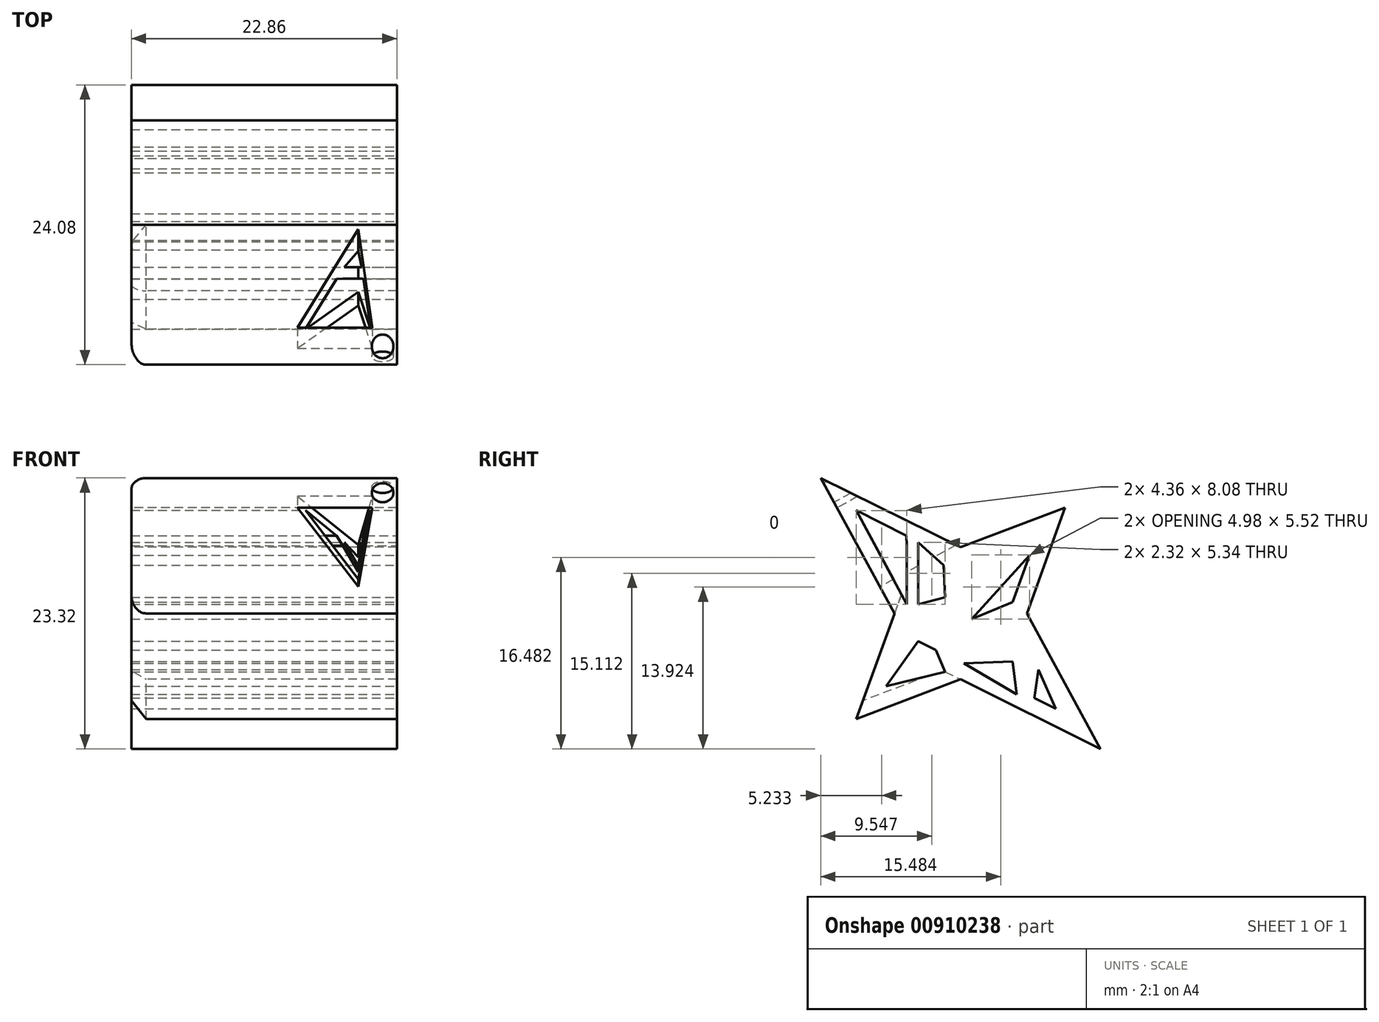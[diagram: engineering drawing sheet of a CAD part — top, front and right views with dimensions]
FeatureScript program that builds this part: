
annotation { "Feature Type Name" : "Feature", "Feature Type Description" : "" }
export const myFeature = defineFeature(function(context is Context, id is Id, definition is map)
    precondition{}
    {
        {
            var Q0;
            Q0=qCreatedBy(makeId("Right.planeOp"),FACE);
            var sketch = newSketch(context, id + "F0", { "sketchPlane" : qUnion([Q0])});
            skPoint(sketch, "E0.middle", {"position": v(0, 0) * mm});
            skLineSegment(sketch, "E1", {"start": v(-12.04, 11.66) * mm, "end": v(-5.68, 0) * mm});
            skLineSegment(sketch, "E2", {"start": v(-8.99, -9.1) * mm, "end": v(-5.68, 0) * mm});
            skLineSegment(sketch, "E3", {"start": v(-8.99, -9.1) * mm, "end": v(0, -5.68) * mm});
            skLineSegment(sketch, "E4", {"start": v(0, -5.68) * mm, "end": v(12.04, -11.66) * mm});
            skLineSegment(sketch, "E5", {"start": v(5.7, 0) * mm, "end": v(12.04, -11.66) * mm});
            skLineSegment(sketch, "E6", {"start": v(5.7, 0) * mm, "end": v(8.99, 9.1) * mm});
            skLineSegment(sketch, "E7", {"start": v(0, 5.7) * mm, "end": v(8.99, 9.1) * mm});
            skLineSegment(sketch, "E8", {"start": v(-12.04, 11.66) * mm, "end": v(0, 5.7) * mm});
            skSolve(sketch);
        }
        {
            var Q0;
            Q0 = qSketchRegion(id + "F0", true);
            extrude(context, id + "F1", {"entities" : qUnion([Q0]), "depth" : 22.86 * mm, "offsetDistance" : 25.4 * mm});
        }
        {
            var Q0;
            Q0=makeQuery(id+"F1.opExtrude","CAP_FACE",FACE,{"disambiguationData":[OSD([sQuery(id+"F0.wireOp",EDGE,"E1"),sQuery(id+"F0.wireOp",EDGE,"E2"),sQuery(id+"F0.wireOp",EDGE,"E3"),sQuery(id+"F0.wireOp",EDGE,"E4"),sQuery(id+"F0.wireOp",EDGE,"E5"),sQuery(id+"F0.wireOp",EDGE,"E6"),sQuery(id+"F0.wireOp",EDGE,"E7"),sQuery(id+"F0.wireOp",EDGE,"E8")])],"isStart":false});
            var sketch = newSketch(context, id + "F2", { "sketchPlane" : qUnion([Q0])});
            skPoint(sketch, "E9.startSnap0", {"position": v(8.87, -5.83) * mm});
            skLineSegment(sketch, "E10", {"start": v(6.69, -4.84) * mm, "end": v(6.34, -7.27) * mm});
            skLineSegment(sketch, "E11", {"start": v(4.84, -6.97) * mm, "end": v(4.47, -4.15) * mm});
            skLineSegment(sketch, "E12", {"start": v(0.3, -4.3) * mm, "end": v(4.47, -4.15) * mm});
            skLineSegment(sketch, "E13", {"start": v(4.84, -3.15) * mm, "end": v(-0.46, -3.15) * mm});
            skLineSegment(sketch, "E14", {"start": v(-0.46, -3.15) * mm, "end": v(4.84, -3.15) * mm});
            skLineSegment(sketch, "E15", {"start": v(4.84, -3.15) * mm, "end": v(4.22, -0.5) * mm});
            skLineSegment(sketch, "E16", {"start": v(-0.46, -3.15) * mm, "end": v(4.22, -0.5) * mm});
            skLineSegment(sketch, "E17", {"start": v(4.47, 0.96) * mm, "end": v(5.93, 5.02) * mm});
            skLineSegment(sketch, "E18", {"start": v(5.93, 5.02) * mm, "end": v(0.95, -0.5) * mm});
            skLineSegment(sketch, "E19", {"start": v(4.47, 0.96) * mm, "end": v(0.95, -0.5) * mm});
            skLineSegment(sketch, "E20", {"start": v(5.2, 6.12) * mm, "end": v(0, 4.16) * mm});
            skLineSegment(sketch, "E21", {"start": v(0, 4.16) * mm, "end": v(5.2, 6.12) * mm});
            skLineSegment(sketch, "E22", {"start": v(5.2, 6.12) * mm, "end": v(0, 1.38) * mm});
            skLineSegment(sketch, "E23", {"start": v(0, 4.16) * mm, "end": v(0, 1.38) * mm});
            skLineSegment(sketch, "E24", {"start": v(-1.33, 1.38) * mm, "end": v(-1.47, 4.16) * mm});
            skLineSegment(sketch, "E25", {"start": v(-1.47, 4.16) * mm, "end": v(-3.65, 6.12) * mm});
            skLineSegment(sketch, "E26", {"start": v(-3.65, 6.12) * mm, "end": v(-3.65, 0.78) * mm});
            skLineSegment(sketch, "E27", {"start": v(-1.33, 1.38) * mm, "end": v(-3.65, 0.78) * mm});
            skLineSegment(sketch, "E28", {"start": v(-1.33, -5.01) * mm, "end": v(-2.14, -3.15) * mm});
            skLineSegment(sketch, "E29", {"start": v(-2.14, -3.15) * mm, "end": v(-3.65, -2.38) * mm});
            skLineSegment(sketch, "E30", {"start": v(-3.65, -2.38) * mm, "end": v(-6.4, -6.26) * mm});
            skLineSegment(sketch, "E31", {"start": v(-6.4, -6.26) * mm, "end": v(-1.33, -5.01) * mm});
            skLineSegment(sketch, "E32", {"start": v(-4.63, 0.78) * mm, "end": v(-4.63, 5.83) * mm});
            skPoint(sketch, "E32.endSnap0", {"position": v(-8.86, 5.83) * mm});
            skLineSegment(sketch, "E33", {"start": v(-4.63, 5.83) * mm, "end": v(-4.66, 6.7) * mm});
            skLineSegment(sketch, "E34", {"start": v(-4.66, 6.7) * mm, "end": v(-8.99, 8.86) * mm});
            skLineSegment(sketch, "E35", {"start": v(-8.99, 8.86) * mm, "end": v(-4.63, 0.78) * mm});
            skLineSegment(sketch, "E36", {"start": v(4.84, -6.97) * mm, "end": v(0.3, -4.3) * mm});
            skLineSegment(sketch, "E37", {"start": v(-8.99, 8.86) * mm, "end": v(-10.17, 8.22) * mm, "construction": true});
            skLineSegment(sketch, "E38", {"start": v(-4.03, 0) * mm, "end": v(-4.63, 0.78) * mm, "construction": true});
            skLineSegment(sketch, "E39", {"start": v(-4.63, 4.78) * mm, "end": v(-3.65, 4.78) * mm, "construction": true});
            skPoint(sketch, "E39.endSnap0", {"position": v(-3.65, 3.45) * mm});
            skLineSegment(sketch, "E40", {"start": v(-1.4, 2.78) * mm, "end": v(0, 2.78) * mm, "construction": true});
            skLineSegment(sketch, "E41", {"start": v(1.53, 2.78) * mm, "end": v(2.73, 1.47) * mm, "construction": true});
            skLineSegment(sketch, "E42", {"start": v(4.47, -1.56) * mm, "end": v(6.31, -1.13) * mm, "construction": true});
            skLineSegment(sketch, "E43", {"start": v(6.34, -7.27) * mm, "end": v(8.19, -8.19) * mm});
            skLineSegment(sketch, "E44", {"start": v(6.69, -4.84) * mm, "end": v(8.19, -8.19) * mm});
            skLineSegment(sketch, "E45", {"start": v(-4.03, 0) * mm, "end": v(-1.14, -2.06) * mm});
            skLineSegment(sketch, "E46", {"start": v(-1.14, -2.06) * mm, "end": v(-4.03, 0) * mm});
            skLineSegment(sketch, "E47", {"start": v(-4.03, 0) * mm, "end": v(-0.2, -0.5) * mm});
            skLineSegment(sketch, "E48", {"start": v(-0.2, -0.5) * mm, "end": v(-1.14, -2.06) * mm});
            skSolve(sketch);
        }
        {
            var Q0;
            Q0=makeQuery(id+"F2.imprint","IMPRINT",FACE,{"disambiguationData":[TD([[makeQuery(id+"F2.imprint","IMPRINT",EDGE,{"derivedFrom":sQuery(id+"F2.wireOp",EDGE,"nE2Qsl0X-DvAB-Qw5M-Smw6-ZWJYBDrrcIoU")}),1.0]])]});
            var Q1;
            Q1=makeQuery(id+"F2.imprint","IMPRINT",FACE,{"disambiguationData":[TD([[makeQuery(id+"F2.imprint","IMPRINT",EDGE,{"derivedFrom":sQuery(id+"F2.wireOp",EDGE,"E11")}),1.0]])]});
            var Q2;
            Q2=makeQuery(id+"F2.imprint","IMPRINT",FACE,{"disambiguationData":[TD([[makeQuery(id+"F2.imprint","IMPRINT",EDGE,{"derivedFrom":sQuery(id+"F2.wireOp",EDGE,"E14")}),1.0]])]});
            var Q3;
            Q3=makeQuery(id+"F2.imprint","IMPRINT",FACE,{"disambiguationData":[TD([[makeQuery(id+"F2.imprint","IMPRINT",EDGE,{"derivedFrom":sQuery(id+"F2.wireOp",EDGE,"E28")}),1.0]])]});
            var Q4;
            Q4=makeQuery(id+"F2.imprint","IMPRINT",FACE,{"disambiguationData":[TD([[makeQuery(id+"F2.imprint","IMPRINT",EDGE,{"derivedFrom":sQuery(id+"F2.wireOp",EDGE,"V6S1NtYD-F1rM-hO7p-zKYz-p3XUJGEGcDZX")}),1.0]])]});
            var Q5;
            Q5=makeQuery(id+"F2.imprint","IMPRINT",FACE,{"disambiguationData":[TD([[makeQuery(id+"F2.imprint","IMPRINT",EDGE,{"derivedFrom":sQuery(id+"F2.wireOp",EDGE,"E24")}),1.0]])]});
            var Q6;
            Q6=makeQuery(id+"F2.imprint","IMPRINT",FACE,{"disambiguationData":[TD([[makeQuery(id+"F2.imprint","IMPRINT",EDGE,{"derivedFrom":sQuery(id+"F2.wireOp",EDGE,"E32")}),1.0]])]});
            var Q7;
            Q7=makeQuery(id+"F2.imprint","IMPRINT",FACE,{"disambiguationData":[TD([[makeQuery(id+"F2.imprint","IMPRINT",EDGE,{"derivedFrom":sQuery(id+"F2.wireOp",EDGE,"1S0bT3UO-28IP-Q8NI-ZD6i-Laru1sXz17AQ")}),1.0]])]});
            var Q8;
            Q8=makeQuery(id+"F2.imprint","IMPRINT",FACE,{"disambiguationData":[TD([[makeQuery(id+"F2.imprint","IMPRINT",EDGE,{"derivedFrom":sQuery(id+"F2.wireOp",EDGE,"E17")}),1.0]])]});
            var Q9;
            Q9=makeQuery(id+"F2.imprint","IMPRINT",FACE,{"disambiguationData":[TD([[makeQuery(id+"F2.imprint","IMPRINT",EDGE,{"derivedFrom":sQuery(id+"F2.wireOp",EDGE,"E21")}),-1.0]])]});
            var Q10;
            Q10=makeQuery(id+"F2.imprint","IMPRINT",FACE,{"disambiguationData":[TD([[makeQuery(id+"F2.imprint","IMPRINT",EDGE,{"derivedFrom":sQuery(id+"F2.wireOp",EDGE,"E46")}),-1.0]])]});
            var Q11;
            Q11=makeQuery(id+"F2.imprint","IMPRINT",FACE,{"disambiguationData":[TD([[makeQuery(id+"F2.imprint","IMPRINT",EDGE,{"derivedFrom":sQuery(id+"F2.wireOp",EDGE,"E10")}),1.0]])]});
            extrude(context, id + "F3", {"entities" : qUnion([Q0, Q1, Q2, Q3, Q4, Q5, Q6, Q7, Q8, Q9, Q10, Q11]), "operationType" : NewBodyOperationType.REMOVE, "endBound" : BoundingType.THROUGH_ALL, "oppositeDirection" : true, "depth" : 25.4 * mm, "offsetDistance" : 25.4 * mm});
        }
        {
            var Q0;
            Q0=makeQuery(id+"F1.opExtrude","SWEPT_FACE",FACE,{"disambiguationData":[OSD([sQuery(id+"F0.wireOp",EDGE,"E1")])]});
            var sketch = newSketch(context, id + "F4", { "sketchPlane" : qUnion([Q0])});
            skLineSegment(sketch, "E49", {"start": v(14.3, 13.08) * mm, "end": v(20.74, 13.08) * mm});
            skLineSegment(sketch, "E50", {"start": v(20.74, 13.08) * mm, "end": v(19.53, 5.35) * mm});
            skLineSegment(sketch, "E51", {"start": v(19.53, 5.35) * mm, "end": v(14.3, 13.08) * mm});
            skSolve(sketch);
        }
        {
            var Q0;
            Q0=makeQuery(id+"F4.imprint","IMPRINT",FACE,{"disambiguationData":[TD([[makeQuery(id+"F4.imprint","IMPRINT",EDGE,{"derivedFrom":sQuery(id+"F4.wireOp",EDGE,"E49")}),-1.0]])]});
            extrude(context, id + "F5", {"entities" : qUnion([Q0]), "operationType" : NewBodyOperationType.REMOVE, "endBound" : BoundingType.THROUGH_ALL, "oppositeDirection" : true, "depth" : 25.4 * mm, "offsetDistance" : 25.4 * mm});
        }
        {
            var Q0;
            Q0=makeQuery(id+"F1.opExtrude","SWEPT_FACE",FACE,{"disambiguationData":[OSD([sQuery(id+"F0.wireOp",EDGE,"E1")])]});
            var sketch = newSketch(context, id + "F6", { "sketchPlane" : qUnion([Q0])});
            skCircle(sketch, "E52", {"center": v(21.62, 14.56) * mm, "radius": 0.93 * mm});
            skSolve(sketch);
        }
        {
            var Q0;
            Q0=makeQuery(id+"F6.imprint","IMPRINT",FACE,{"disambiguationData":[TD([[makeQuery(id+"F6.imprint","IMPRINT",EDGE,{"derivedFrom":sQuery(id+"F6.wireOp",EDGE,"E52")}),1.0]])]});
            extrude(context, id + "F7", {"entities" : qUnion([Q0]), "operationType" : NewBodyOperationType.REMOVE, "endBound" : BoundingType.THROUGH_ALL, "oppositeDirection" : true, "depth" : 25.4 * mm, "offsetDistance" : 25.4 * mm});
        }
        {
            var Q0;
            Q0=makeQuery(id+"F1.opExtrude","CAP_EDGE",EDGE,{"disambiguationData":[OSD([sQuery(id+"F0.wireOp",EDGE,"E1")])],"isStart":true});
            fillet(context, id + "F8", {"entities" : qUnion([Q0]), "tangentPropagation" : true, "radius" : 1.27 * mm, "defaultsChanged" : true, "vertexSettings" : [], "allowEdgeOverflow" : false});
        }
        {
            var Q0;
            Q0=makeQuery(id+"F1.opExtrude","CAP_EDGE",EDGE,{"disambiguationData":[OSD([sQuery(id+"F0.wireOp",EDGE,"E3")])],"isStart":true});
            chamfer(context, id + "F9", {"entities" : qUnion([Q0]), "width" : 1.27 * mm, "tangentPropagation" : true});
        }
    });
